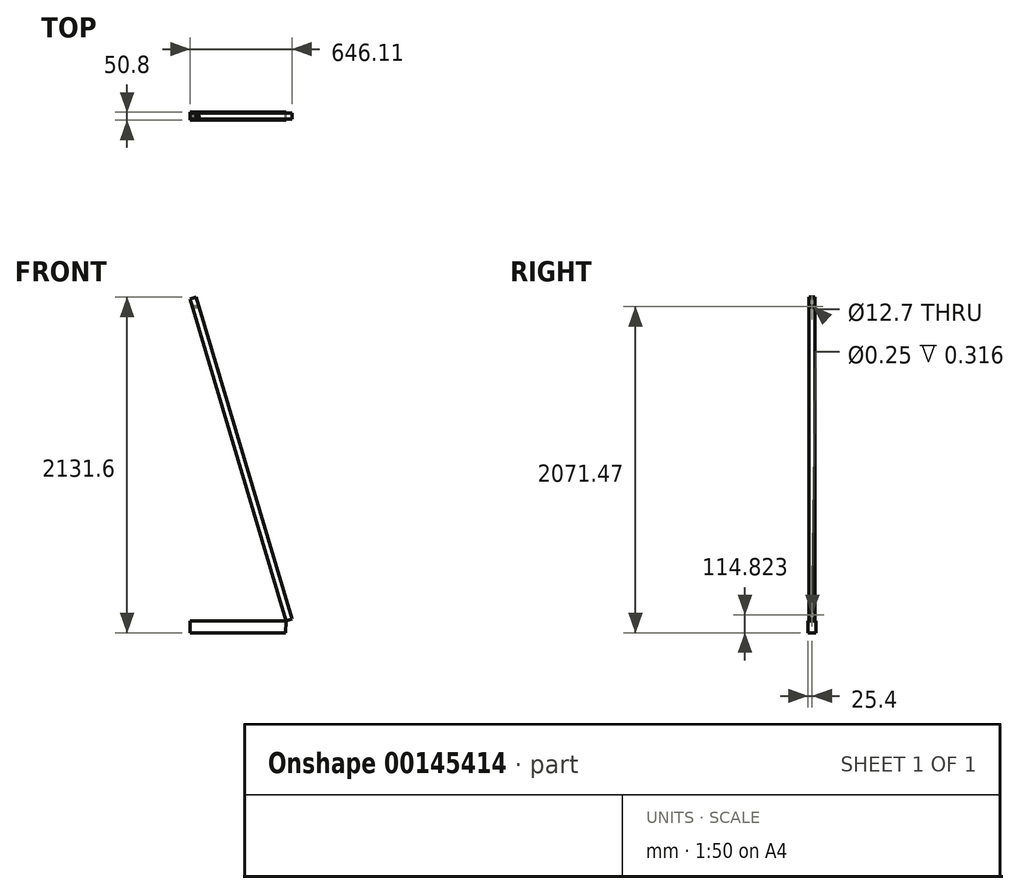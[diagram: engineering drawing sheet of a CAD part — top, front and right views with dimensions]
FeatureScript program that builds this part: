
annotation { "Feature Type Name" : "Feature", "Feature Type Description" : "" }
export const myFeature = defineFeature(function(context is Context, id is Id, definition is map)
    precondition{}
    {
        {
            var Q0;
            Q0=qCreatedBy(makeId("Front.planeOp"),FACE);
            var sketch = newSketch(context, id + "F0", { "sketchPlane" : qUnion([Q0])});
            skLineSegment(sketch, "E0", {"start": v(-558.4, 1106.8) * mm, "end": v(-558.4, -937.85) * mm});
            skLineSegment(sketch, "E1", {"start": v(-558.4, -937.85) * mm, "end": v(51.2, -937.85) * mm});
            skLineSegment(sketch, "E2", {"start": v(51.2, -937.85) * mm, "end": v(-558.4, 1106.8) * mm});
            skPoint(sketch, "E3", {"position": v(51.2, -937.85) * mm});
            skLineSegment(sketch, "E4", {"start": v(51.2, -937.85) * mm, "end": v(87.72, -926.97) * mm});
            skLineSegment(sketch, "E5", {"start": v(-558.4, 1106.8) * mm, "end": v(-521.88, 1117.7) * mm});
            skLineSegment(sketch, "E6", {"start": v(-521.88, 1117.7) * mm, "end": v(87.72, -926.97) * mm});
            skPoint(sketch, "E7", {"position": v(-503.74, 1056.84) * mm});
            skLineSegment(sketch, "E8", {"start": v(-503.74, 1056.84) * mm, "end": v(-558.4, 1056.84) * mm});
            skLineSegment(sketch, "E9", {"start": v(-558.4, -937.85) * mm, "end": v(-558.4, -1013.9) * mm});
            skLineSegment(sketch, "E10", {"start": v(-558.4, -1013.9) * mm, "end": v(49.64, -1013.9) * mm});
            skLineSegment(sketch, "E11", {"start": v(49.64, -1013.9) * mm, "end": v(51.2, -937.85) * mm});
            skSolve(sketch);
        }
        {
            var Q0;
            Q0=makeQuery(id+"F0.imprint","IMPRINT",FACE,{"disambiguationData":[TD([[makeQuery(id+"F0.imprint","IMPRINT",EDGE,{"derivedFrom":sQuery(id+"F0.wireOp",EDGE,"E2")}),-1.0]])]});
            extrude(context, id + "F1", {"entities" : qUnion([Q0]), "endBound" : BoundingType.SYMMETRIC, "depth" : 38.1 * mm});
        }
        {
            var Q0;
            Q0=qCreatedBy(makeId("Right.planeOp"),FACE);
            var sketch = newSketch(context, id + "F2", { "sketchPlane" : qUnion([Q0])});
            skPoint(sketch, "E12", {"position": v(0, 1057.56) * mm});
            skSolve(sketch);
        }
        {
            var Q0;
            Q0=sQuery(id+"F2.wireOp",VERTEX,"E12");
            var Q1;
            Q1=makeQuery(id+"F1.opExtrude","SWEPT_BODY",BODY,{"disambiguationData":[OSD([sQuery(id+"F0.wireOp",EDGE,"E2"),sQuery(id+"F0.wireOp",EDGE,"E4"),sQuery(id+"F0.wireOp",EDGE,"E5"),sQuery(id+"F0.wireOp",EDGE,"E6")])]});
            hole(context, id + "F3", {"style" : HoleStyle.SIMPLE, "endStyle" : HoleEndStyle.BLIND, "holeDiameter" : 12.7 * mm, "holeDepth" : 609.6 * mm, "locations" : qUnion([Q0]), "scope" : qUnion([Q1])});
        }
        {
            var Q0;
            Q0=makeQuery(id+"F0.imprint","IMPRINT",FACE,{"disambiguationData":[TD([[makeQuery(id+"F0.imprint","IMPRINT",EDGE,{"derivedFrom":sQuery(id+"F0.wireOp",EDGE,"E1")}),-1.0]])]});
            extrude(context, id + "F4", {"entities" : qUnion([Q0]), "endBound" : BoundingType.SYMMETRIC, "depth" : 50.8 * mm});
        }
        {
            var Q0;
            Q0=qCreatedBy(makeId("Right.planeOp"),FACE);
            cPlane(context, id + "F5", {"entities" : qUnion([Q0]), "cplaneType" : CPlaneType.OFFSET, "offset" : 39.93 * mm, "width" : 152.4 * mm, "height" : 152.4 * mm});
        }
        {
            var Q0;
            Q0=qCreatedBy(id+"F5.planeOp",FACE);
            var sketch = newSketch(context, id + "F6", { "sketchPlane" : qUnion([Q0])});
            skPoint(sketch, "E13", {"position": v(0, -899.09) * mm});
            skSolve(sketch);
        }
        {
            var Q0;
            Q0=sQuery(id+"F6.wireOp",VERTEX,"E13");
            var Q1;
            Q1=makeQuery(id+"F1.opExtrude","SWEPT_BODY",BODY,{"disambiguationData":[OSD([sQuery(id+"F0.wireOp",EDGE,"E2"),sQuery(id+"F0.wireOp",EDGE,"E4"),sQuery(id+"F0.wireOp",EDGE,"E5"),sQuery(id+"F0.wireOp",EDGE,"E6")])]});
            hole(context, id + "F7", {"style" : HoleStyle.SIMPLE, "endStyle" : HoleEndStyle.THROUGH, "holeDiameter" : 0.25 * mm, "locations" : qUnion([Q0]), "scope" : qUnion([Q1]), "isTappedThrough" : true});
        }
    });
